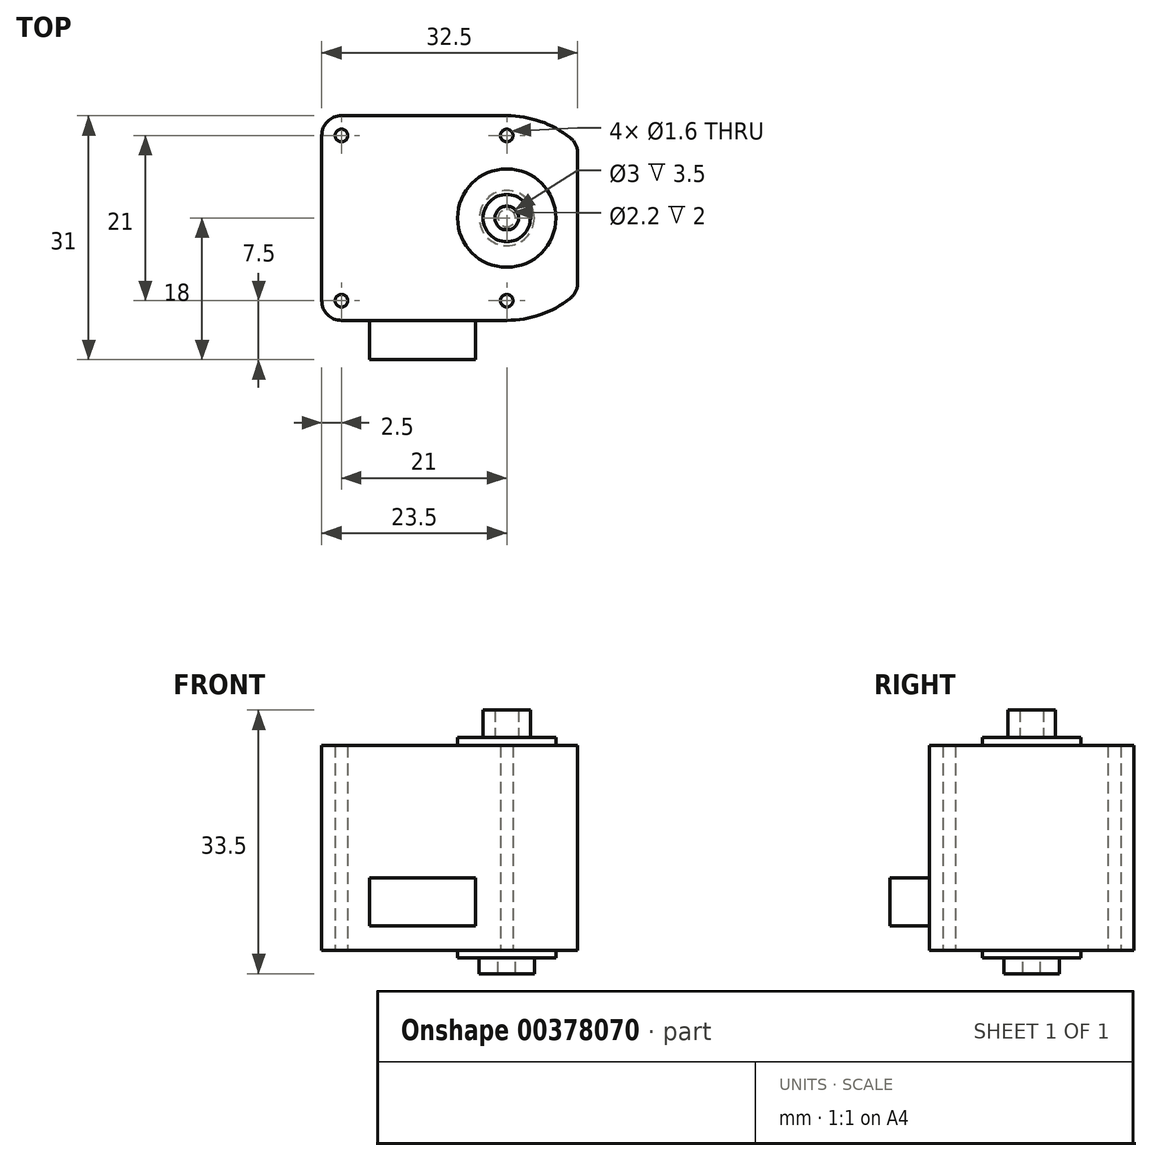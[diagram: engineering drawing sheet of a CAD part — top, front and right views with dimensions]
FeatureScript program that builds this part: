
annotation { "Feature Type Name" : "Feature", "Feature Type Description" : "" }
export const myFeature = defineFeature(function(context is Context, id is Id, definition is map)
    precondition{}
    {
        {
            var Q0;
            Q0=qCreatedBy(makeId("Top.planeOp"),FACE);
            var sketch = newSketch(context, id + "F0", { "sketchPlane" : qUnion([Q0])});
            skLineSegment(sketch, "E0", {"start": v(0, 0) * mm, "end": v(-23.5, 0) * mm, "construction": true});
            skLineSegment(sketch, "E1", {"start": v(-23.5, 0) * mm, "end": v(-23.5, 10.5) * mm});
            skLineSegment(sketch, "E2", {"start": v(-21, 13) * mm, "end": v(9, 13) * mm, "construction": true});
            skLineSegment(sketch, "E3", {"start": v(9, 13) * mm, "end": v(9, 0) * mm, "construction": true});
            skLineSegment(sketch, "E4", {"start": v(9, 0) * mm, "end": v(0, 0) * mm, "construction": true});
            skLineSegment(sketch, "E5", {"start": v(-21, 0) * mm, "end": v(-21, 10.5) * mm, "construction": true});
            skLineSegment(sketch, "E6", {"start": v(-21, 10.5) * mm, "end": v(0, 10.5) * mm, "construction": true});
            skLineSegment(sketch, "E7", {"start": v(0, 10.5) * mm, "end": v(0, 0) * mm, "construction": true});
            skPoint(sketch, "E8.visualSharp", {"position": v(-23.5, 13) * mm});
            skArc(sketch, "E8.filletArc", {"start": v(-21, 13) * mm, "mid": v(-22.77, 12.27) * mm, "end": v(-23.5, 10.5) * mm});
            skCircle(sketch, "E9", {"center": v(-21, 10.5) * mm, "radius": 0.8 * mm});
            skCircle(sketch, "E10", {"center": v(0, 10.5) * mm, "radius": 0.8 * mm});
            skArc(sketch, "E11", {"start": v(0, 13) * mm, "mid": v(4.26, 12.28) * mm, "end": v(8.05, 10.2) * mm});
            skLineSegment(sketch, "E12", {"start": v(-21, 13) * mm, "end": v(0, 13) * mm});
            skLineSegment(sketch, "E13", {"start": v(9, 8.25) * mm, "end": v(9, 0) * mm});
            skPoint(sketch, "E14.visualSharp", {"position": v(9, 9.38) * mm});
            skArc(sketch, "E14.filletArc", {"start": v(9, 8.25) * mm, "mid": v(8.75, 9.34) * mm, "end": v(8.05, 10.2) * mm});
            skLineSegment(sketch, "E15.MirrorCS", {"start": v(-23.5, 0) * mm, "end": v(-23.5, -10.5) * mm});
            skArc(sketch, "E16.MirrorCS", {"start": v(-21, -13) * mm, "mid": v(-22.77, -12.27) * mm, "end": v(-23.5, -10.5) * mm});
            skLineSegment(sketch, "E17.MirrorCS", {"start": v(-21, -13) * mm, "end": v(0, -13) * mm});
            skArc(sketch, "E18.MirrorCS", {"start": v(0, -13) * mm, "mid": v(4.26, -12.28) * mm, "end": v(8.05, -10.2) * mm});
            skArc(sketch, "E19.MirrorCS", {"start": v(9, -8.25) * mm, "mid": v(8.75, -9.34) * mm, "end": v(8.05, -10.2) * mm});
            skLineSegment(sketch, "E20.MirrorCS", {"start": v(9, -8.25) * mm, "end": v(9, 0) * mm});
            skCircle(sketch, "E21.MirrorC", {"center": v(0, -10.5) * mm, "radius": 0.8 * mm});
            skCircle(sketch, "E22.MirrorC", {"center": v(-21, -10.5) * mm, "radius": 0.8 * mm});
            skSolve(sketch);
        }
        {
            var Q0;
            Q0=makeQuery(id+"F0.imprint","IMPRINT",FACE,{"disambiguationData":[TD([[makeQuery(id+"F0.imprint","IMPRINT",EDGE,{"derivedFrom":sQuery(id+"F0.wireOp",EDGE,"E1")}),-1.0]])]});
            extrude(context, id + "F1", {"entities" : qUnion([Q0]), "endBound" : BoundingType.SYMMETRIC, "depth" : 26 * mm});
        }
        {
            var Q0;
            Q0=makeQuery(id+"F1.opExtrude","CAP_FACE",FACE,{"disambiguationData":[OSD([sQuery(id+"F0.wireOp",EDGE,"E1"),sQuery(id+"F0.wireOp",EDGE,"E8.filletArc"),sQuery(id+"F0.wireOp",EDGE,"E9"),sQuery(id+"F0.wireOp",EDGE,"E10"),sQuery(id+"F0.wireOp",EDGE,"E11"),sQuery(id+"F0.wireOp",EDGE,"E12"),sQuery(id+"F0.wireOp",EDGE,"E13"),sQuery(id+"F0.wireOp",EDGE,"E14.filletArc"),sQuery(id+"F0.wireOp",EDGE,"E15.MirrorCS"),sQuery(id+"F0.wireOp",EDGE,"E16.MirrorCS"),sQuery(id+"F0.wireOp",EDGE,"E17.MirrorCS"),sQuery(id+"F0.wireOp",EDGE,"E18.MirrorCS"),sQuery(id+"F0.wireOp",EDGE,"E19.MirrorCS"),sQuery(id+"F0.wireOp",EDGE,"E20.MirrorCS"),sQuery(id+"F0.wireOp",EDGE,"E21.MirrorC"),sQuery(id+"F0.wireOp",EDGE,"E22.MirrorC")])],"isStart":false});
            var sketch = newSketch(context, id + "F2", { "sketchPlane" : qUnion([Q0])});
            skCircle(sketch, "E23", {"center": v(0, 0) * mm, "radius": 6.25 * mm});
            skSolve(sketch);
        }
        {
            var Q0;
            Q0=makeQuery(id+"F2.imprint","IMPRINT",FACE,{"disambiguationData":[TD([[makeQuery(id+"F2.imprint","IMPRINT",EDGE,{"derivedFrom":sQuery(id+"F2.wireOp",EDGE,"E23")}),1.0]])]});
            extrude(context, id + "F3", {"entities" : qUnion([Q0]), "operationType" : NewBodyOperationType.ADD, "depth" : 1 * mm, "hasSecondDirection" : true, "secondDirectionOppositeDirection" : true, "secondDirectionDepth" : (26 + 1) * mm});
        }
        {
            var Q0;
            Q0=makeQuery(id+"F3.opExtrude","CAP_FACE",FACE,{"disambiguationData":[OSD([sQuery(id+"F2.wireOp",EDGE,"E23")])],"isStart":false});
            var sketch = newSketch(context, id + "F4", { "sketchPlane" : qUnion([Q0])});
            skCircle(sketch, "E24", {"center": v(0, 0) * mm, "radius": 3 * mm});
            skCircle(sketch, "E25", {"center": v(0, 0) * mm, "radius": 1.5 * mm});
            skSolve(sketch);
        }
        {
            var Q0;
            Q0=makeQuery(id+"F4.imprint","IMPRINT",FACE,{"disambiguationData":[TD([[makeQuery(id+"F4.imprint","IMPRINT",EDGE,{"derivedFrom":sQuery(id+"F4.wireOp",EDGE,"E24")}),1.0]])]});
            extrude(context, id + "F5", {"entities" : qUnion([Q0]), "operationType" : NewBodyOperationType.ADD, "depth" : 3.5 * mm});
        }
        {
            var Q0;
            Q0=makeQuery(id+"F3.opExtrude","CAP_FACE",FACE,{"disambiguationData":[OSD([sQuery(id+"F2.wireOp",EDGE,"E23")])],"isStart":true});
            var sketch = newSketch(context, id + "F6", { "sketchPlane" : qUnion([Q0])});
            skCircle(sketch, "E26", {"center": v(0, 0) * mm, "radius": 3.5 * mm});
            skCircle(sketch, "E27", {"center": v(0, 0) * mm, "radius": 1.1 * mm});
            skSolve(sketch);
        }
        {
            var Q0;
            Q0=qSketchRegion(id+"F6",true);
            extrude(context, id + "F7", {"entities" : qUnion([Q0]), "operationType" : NewBodyOperationType.ADD, "depth" : (3 - 1) * mm});
        }
        {
            var Q0;
            Q0=makeQuery(id+"F1.opExtrude","SWEPT_FACE",FACE,{"disambiguationData":[OSD([sQuery(id+"F0.wireOp",EDGE,"E17.MirrorCS")])]});
            var sketch = newSketch(context, id + "F8", { "sketchPlane" : qUnion([Q0])});
            skLineSegment(sketch, "E28", {"start": v(-7.25, -13) * mm, "end": v(-7.25, 13) * mm, "construction": true});
            skLineSegment(sketch, "E29.bottom", {"start": v(-4, -3.8) * mm, "end": v(-17.45, -3.8) * mm});
            skLineSegment(sketch, "E29.top", {"start": v(-4, -9.9) * mm, "end": v(-17.45, -9.9) * mm});
            skLineSegment(sketch, "E29.left", {"start": v(-4, -3.8) * mm, "end": v(-4, -9.9) * mm});
            skLineSegment(sketch, "E29.right", {"start": v(-17.45, -3.8) * mm, "end": v(-17.45, -9.9) * mm});
            skPoint(sketch, "E29.middle", {"position": v(-10.72, -6.85) * mm});
            skSolve(sketch);
        }
        {
            var Q0;
            Q0=qSketchRegion(id+"F8",true);
            extrude(context, id + "F9", {"entities" : qUnion([Q0]), "operationType" : NewBodyOperationType.ADD, "depth" : 5 * mm});
        }
    });
